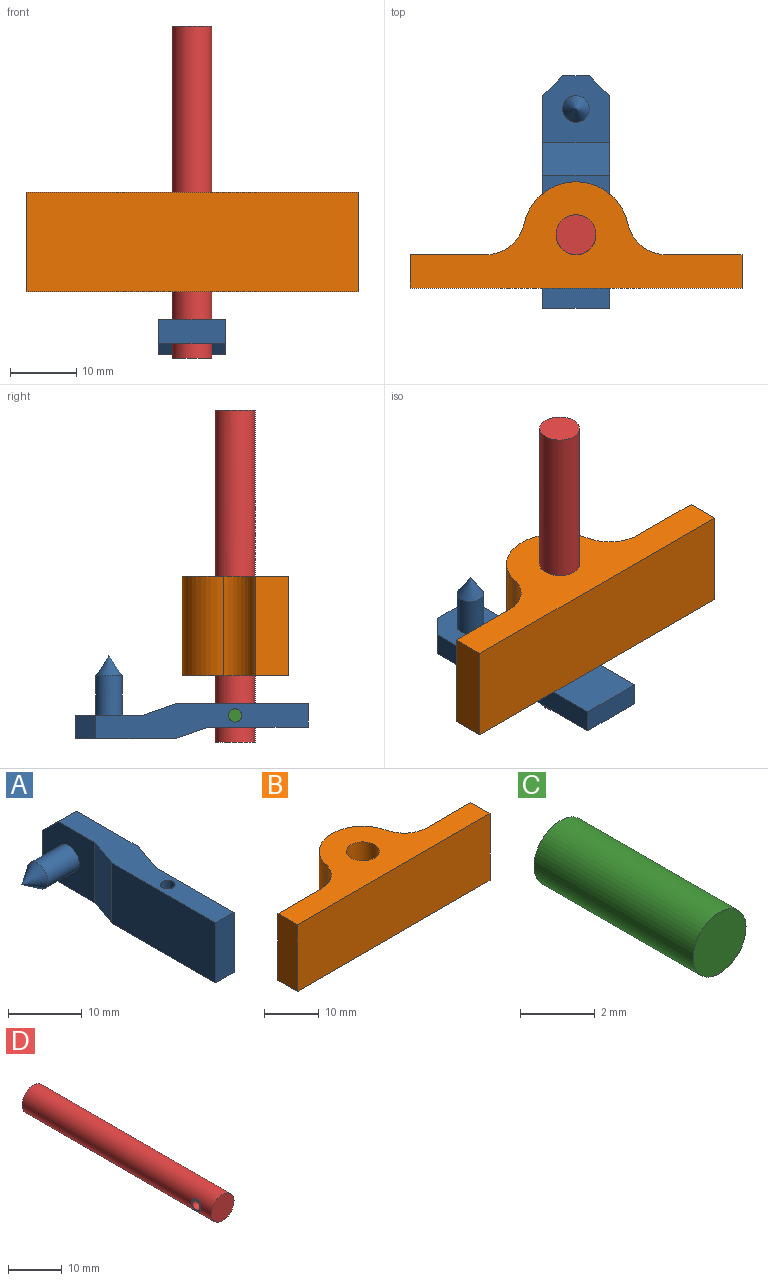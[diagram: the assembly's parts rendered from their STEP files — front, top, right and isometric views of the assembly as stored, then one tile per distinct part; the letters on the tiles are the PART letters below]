
ASSEMBLY  parts=4 mates=5
PART A: 15 faces, bbox 12.5x35x10 mm
  f0: plane 20x10mm, normal (-1,0,0), area 200mm2, adj f1,f6,f7,f9
  f1: plane 10x3.5mm, normal (0,-1,0), area 35mm2, adj f0,f2,f6,f7
  f2: plane 15x10mm, normal (1,0,0), area 150mm2, adj f1,f6,f7,f8
  f3: plane 15x10mm, normal (1,0,0), area 141mm2, adj f4,f6,f7,f8,f13,f14
  f4: plane 4x3.5mm, normal (0,1,0), area 14mm2, adj f3,f5,f13,f14
  f5: plane 10x10mm, normal (-1,0,0), area 78.4mm2, adj f4,f6,f7,f9,f11,f13,f14
  f6: plane 32x5.25mm, normal (0,0,1), area 117.6mm2, adj f0,f1,f2,f3,f5,f8,f9,f10
  f7: plane 32x5.25mm, normal (0,0,-1), area 117.6mm2, adj f0,f1,f2,f3,f5,f8,f9,f10
  f8: plane 10x5mm, normal (0.94,-0.33,0), area 53mm2, adj f2,f3,f6,f7
  f9: plane 10x5mm, normal (-0.94,0.33,0), area 53mm2, adj f0,f5,f6,f7
  f10: cylinder r=1mm len=10mm, axis (0,0,1), area 62.8mm2, adj f6,f7
  f11: cylinder r=2mm len=6mm, axis (1,0,0), area 75.4mm2, adj f5,f12
  f12: cone r=2mm half-angle=33.7deg, axis (1,0,0), area 22.7mm2, adj f11
  f13: plane 3.5x3mm, normal (0,0.71,0.71), area 14.8mm2, adj f3,f4,f5,f6
  f14: plane 3.5x3mm, normal (0,0.71,-0.71), area 14.8mm2, adj f3,f4,f5,f7
PART B: 11 faces, bbox 50x16x15 mm
  f0: plane 15x5mm, normal (-1,0,0), area 75mm2, adj f1,f8,f9,f10
  f1: plane 50x15mm, normal (0,-1,0), area 750mm2, adj f0,f2,f9,f10
  f2: plane 15x5mm, normal (1,0,0), area 75mm2, adj f1,f3,f9,f10
  f3: plane 15x11.33mm, normal (0,1,0), area 169.9mm2, adj f2,f4,f9,f10
  f4: cylinder r=6mm len=15mm, axis (0,0,-1), area 121.9mm2, adj f3,f5,f9,f10
  f5: cylinder r=8mm len=15.63mm, axis (0,0,-1), area 325.2mm2, adj f4,f6,f9,f10
  f6: cylinder r=6mm len=15mm, axis (0,0,-1), area 121.9mm2, adj f5,f8,f9,f10
  f7: cylinder r=3mm len=15mm, axis (0,0,-1), area 282.7mm2, adj f9,f10
  f8: plane 15x11.33mm, normal (0,1,0), area 169.9mm2, adj f0,f6,f9,f10
  f9: plane 50x16mm, normal (0,0,1), area 382.7mm2, adj f0,f1,f2,f3,f4,f5,f6,f7
  f10: plane 50x16mm, normal (0,0,-1), area 382.7mm2, adj f0,f1,f2,f3,f4,f5,f6,f7
PART C: 3 faces, bbox 2x6x2 mm
  f0: cylinder r=1mm len=6mm, axis (0,1,0), area 37.7mm2, adj f1,f2
  f1: plane 2x2mm, normal (0,-1,0), area 3.1mm2, adj f0
  f2: plane 2x2mm, normal (0,1,0), area 3.1mm2, adj f0
PART D: 10 faces, bbox 6x50x6 mm
  f0: cylinder r=3mm len=50mm, axis (0,1,0), area 932.1mm2, adj f1,f2,f4,f5,f6,f7
  f1: plane 6x6mm, normal (0,-1,0), area 28.3mm2, adj f0
  f2: plane 6x6mm, normal (0,1,0), area 28.3mm2, adj f0
  f3: plane 2.54x2.54mm, normal (-1,0,0), area 1.9mm2, adj f4,f5,f9
  f4: cylinder r=1.27mm len=2.54mm, axis (-1,0,0), area 0.6mm2, adj f0,f3
  f5: cylinder r=1.27mm len=2.54mm, axis (-1,0,0), area 0.6mm2, adj f0,f3
  f6: cylinder r=1.27mm len=2.54mm, axis (-1,0,0), area 0.6mm2, adj f0,f8
  f7: cylinder r=1.27mm len=2.54mm, axis (-1,0,0), area 0.6mm2, adj f0,f8
  f8: plane 2.54x2.54mm, normal (1,0,0), area 1.9mm2, adj f6,f7,f9
  f9: cylinder r=1mm len=6mm, axis (-1,0,0), area 37.7mm2, adj f3,f8
PLACE A rot(axis=(0,1,0),90deg) t=(20,-8,-4.25)mm
PLACE B at identity fixed
PLACE C rot(axis=(0,0,1),90deg) t=(22,3,-6)mm
PLACE D rot(axis=(1,0,0),90deg) t=(25,3,40)mm
MATE revolute C.f0 <-> D.f4  axis (1,0,0) through (28,3,-6)mm
MATE revolute D.f4 <-> A.f10  axis (1,0,0) through (28,3,-6)mm
MATE parallel A.f1 <-> B.f1  axis (0,-1,0) through (25,-8,-6)mm
MATE revolute D.f0 <-> B.f5  axis (0,0,1) through (25,3,15)mm
MATE parallel A.f2 <-> B.f5  axis (0,0,-1) through (25,-0.5,-7.75)mm
